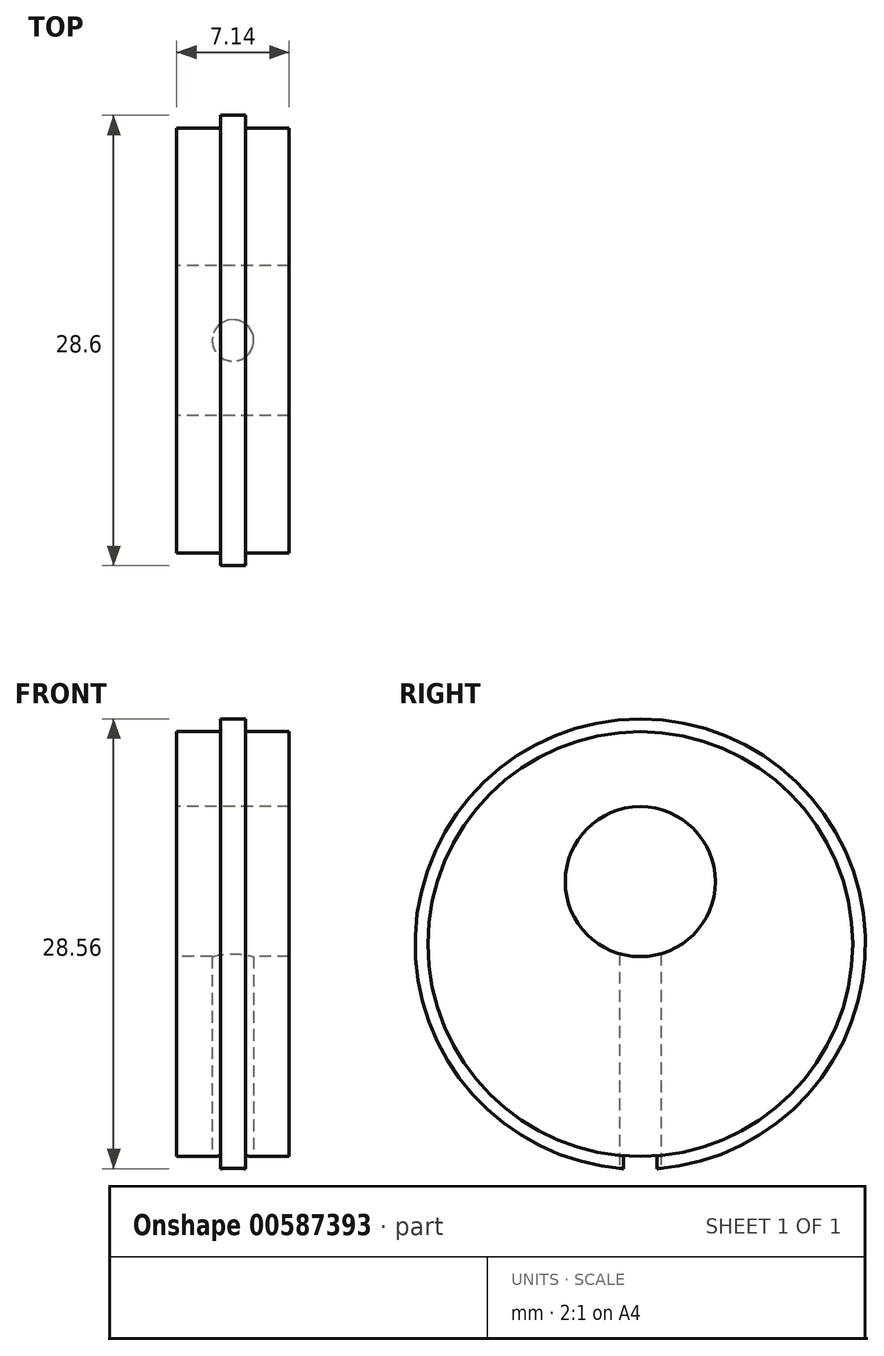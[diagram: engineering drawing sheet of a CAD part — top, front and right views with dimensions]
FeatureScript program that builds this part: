
annotation { "Feature Type Name" : "Feature", "Feature Type Description" : "" }
export const myFeature = defineFeature(function(context is Context, id is Id, definition is map)
    precondition{}
    {
        {
            var Q0;
            Q0=qCreatedBy(makeId("Front.planeOp"),FACE);
            var sketch = newSketch(context, id + "F0", { "sketchPlane" : qUnion([Q0])});
            skLineSegment(sketch, "E0", {"start": v(0, 17.65) * mm, "end": v(0, -17.58) * mm, "construction": true});
            skLineSegment(sketch, "E1", {"start": v(8.35, 0) * mm, "end": v(-9.26, 0) * mm, "construction": true});
            skLineSegment(sketch, "E2", {"start": v(-3.57, 0) * mm, "end": v(-3.57, 13.5) * mm});
            skLineSegment(sketch, "E3", {"start": v(-3.57, 13.5) * mm, "end": v(14.3, 13.5) * mm, "construction": true});
            skLineSegment(sketch, "E4", {"start": v(-3.57, 13.5) * mm, "end": v(-0.8, 13.5) * mm});
            skLineSegment(sketch, "E5", {"start": v(-0.8, 13.5) * mm, "end": v(-0.8, 14.3) * mm});
            skLineSegment(sketch, "E6", {"start": v(-0.8, 14.3) * mm, "end": v(0.8, 14.3) * mm});
            skLineSegment(sketch, "E7", {"start": v(0.8, 14.3) * mm, "end": v(0.8, 13.5) * mm});
            skLineSegment(sketch, "E8", {"start": v(0.8, 13.5) * mm, "end": v(3.57, 13.5) * mm});
            skLineSegment(sketch, "E9", {"start": v(3.57, 13.5) * mm, "end": v(3.57, 0) * mm});
            skLineSegment(sketch, "E10", {"start": v(-3.57, 0) * mm, "end": v(3.57, 0) * mm});
            skSolve(sketch);
        }
        {
            var Q0;
            Q0=makeQuery(id+"F0.imprint","IMPRINT",FACE,{"disambiguationData":[TD([[makeQuery(id+"F0.imprint","IMPRINT",EDGE,{"derivedFrom":sQuery(id+"F0.wireOp",EDGE,"E2")}),-1.0]])]});
            var Q1;
            Q1=sQuery(id+"F0.wireOp",EDGE,"E10");
            revolve(context, id + "F1", {"entities" : qUnion([Q0]), "axis" : qUnion([Q1]), "revolveType" : RevolveType.FULL});
        }
        {
            var Q0;
            Q0=makeQuery(id+"F1.opRevolve","SWEPT_FACE",FACE,{"disambiguationData":[OSD([sQuery(id+"F0.wireOp",EDGE,"E2")])]});
            var sketch = newSketch(context, id + "F2", { "sketchPlane" : qUnion([Q0])});
            skLineSegment(sketch, "E11", {"start": v(0, -6.42) * mm, "end": v(0, 8.84) * mm, "construction": true});
            skLineSegment(sketch, "E12", {"start": v(1.52, 0) * mm, "end": v(-2.75, 0) * mm, "construction": true});
            skLineSegment(sketch, "E13", {"start": v(-2.34, 3.97) * mm, "end": v(2.5, 3.97) * mm, "construction": true});
            skCircle(sketch, "E14", {"center": v(0, 3.97) * mm, "radius": 4.76 * mm});
            skSolve(sketch);
        }
        {
            var Q0;
            Q0=makeQuery(id+"F2.imprint","IMPRINT",FACE,{"disambiguationData":[TD([[makeQuery(id+"F2.imprint","IMPRINT",EDGE,{"derivedFrom":sQuery(id+"F2.wireOp",EDGE,"E14")}),1.0]])]});
            extrude(context, id + "F3", {"entities" : qUnion([Q0]), "operationType" : NewBodyOperationType.REMOVE, "endBound" : BoundingType.THROUGH_ALL, "oppositeDirection" : true, "depth" : 25.4 * mm, "offsetDistance" : 25.4 * mm});
        }
        {
            var Q0;
            Q0=qCreatedBy(makeId("Top.planeOp"),FACE);
            cPlane(context, id + "F4", {"entities" : qUnion([Q0]), "cplaneType" : CPlaneType.OFFSET, "offset" : 14.48 * mm, "oppositeDirection" : true, "width" : 152.4 * mm, "height" : 152.4 * mm});
        }
        {
            var Q0;
            Q0=qCreatedBy(id+"F4.planeOp",FACE);
            var sketch = newSketch(context, id + "F5", { "sketchPlane" : qUnion([Q0])});
            skCircle(sketch, "E15", {"center": v(0, 0) * mm, "radius": 1.32 * mm});
            skSolve(sketch);
        }
        {
            var Q0;
            Q0=makeQuery(id+"F5.imprint","IMPRINT",FACE,{"disambiguationData":[TD([[makeQuery(id+"F5.imprint","IMPRINT",EDGE,{"derivedFrom":sQuery(id+"F5.wireOp",EDGE,"E15")}),1.0]])]});
            extrude(context, id + "F6", {"entities" : qUnion([Q0]), "operationType" : NewBodyOperationType.REMOVE, "depth" : 14.29 * mm, "offsetDistance" : 25.4 * mm});
        }
    });
